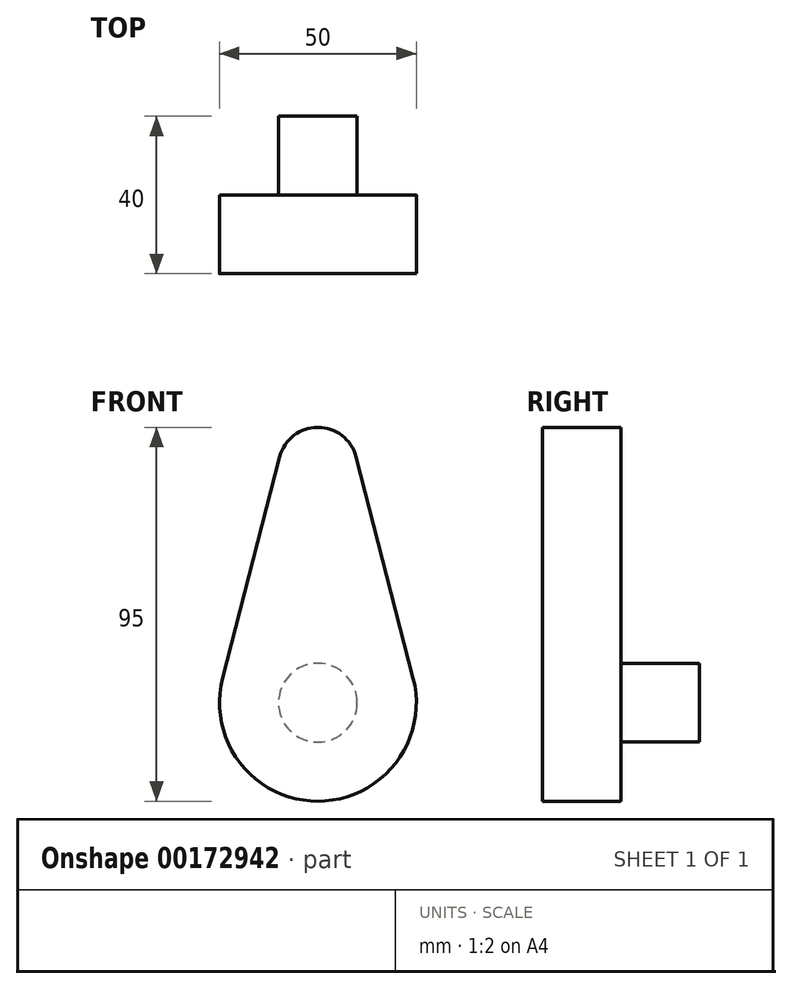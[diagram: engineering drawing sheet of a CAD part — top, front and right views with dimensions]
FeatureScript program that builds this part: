
annotation { "Feature Type Name" : "Feature", "Feature Type Description" : "" }
export const myFeature = defineFeature(function(context is Context, id is Id, definition is map)
    precondition{}
    {
        {
            var Q0;
            Q0=qCreatedBy(makeId("Front.planeOp"),FACE);
            var sketch = newSketch(context, id + "F0", { "sketchPlane" : qUnion([Q0])});
            skCircle(sketch, "E0", {"center": v(0, 0) * mm, "radius": 25 * mm});
            skCircle(sketch, "E1", {"center": v(0, 60) * mm, "radius": 10 * mm});
            skLineSegment(sketch, "E2", {"start": v(-24.2, 6.25) * mm, "end": v(-9.68, 62.5) * mm});
            skLineSegment(sketch, "E3.MirrorCS", {"start": v(24.2, 6.25) * mm, "end": v(9.68, 62.5) * mm});
            skLineSegment(sketch, "E4", {"start": v(0, 0) * mm, "end": v(0, 60) * mm, "construction": true});
            skSolve(sketch);
        }
        {
            var Q0;
            Q0 = qSketchRegion(id + "F0", true);
            extrude(context, id + "F1", {"entities" : qUnion([Q0]), "depth" : 20 * mm});
        }
        {
            var Q0;
            Q0=makeQuery(id+"F1.opExtrude","CAP_FACE",FACE,{"disambiguationData":[OSD([sQuery(id+"F0.wireOp",EDGE,"E0"),sQuery(id+"F0.wireOp",EDGE,"E1"),sQuery(id+"F0.wireOp",EDGE,"E2"),sQuery(id+"F0.wireOp",EDGE,"E3.MirrorCS")])],"isStart":true});
            var sketch = newSketch(context, id + "F2", { "sketchPlane" : qUnion([Q0])});
            skCircle(sketch, "E5", {"center": v(0, 0) * mm, "radius": 10 * mm});
            skSolve(sketch);
        }
        {
            var Q0;
            Q0 = qSketchRegion(id + "F2", true);
            extrude(context, id + "F3", {"entities" : qUnion([Q0]), "operationType" : NewBodyOperationType.ADD, "depth" : 20 * mm});
        }
    });
